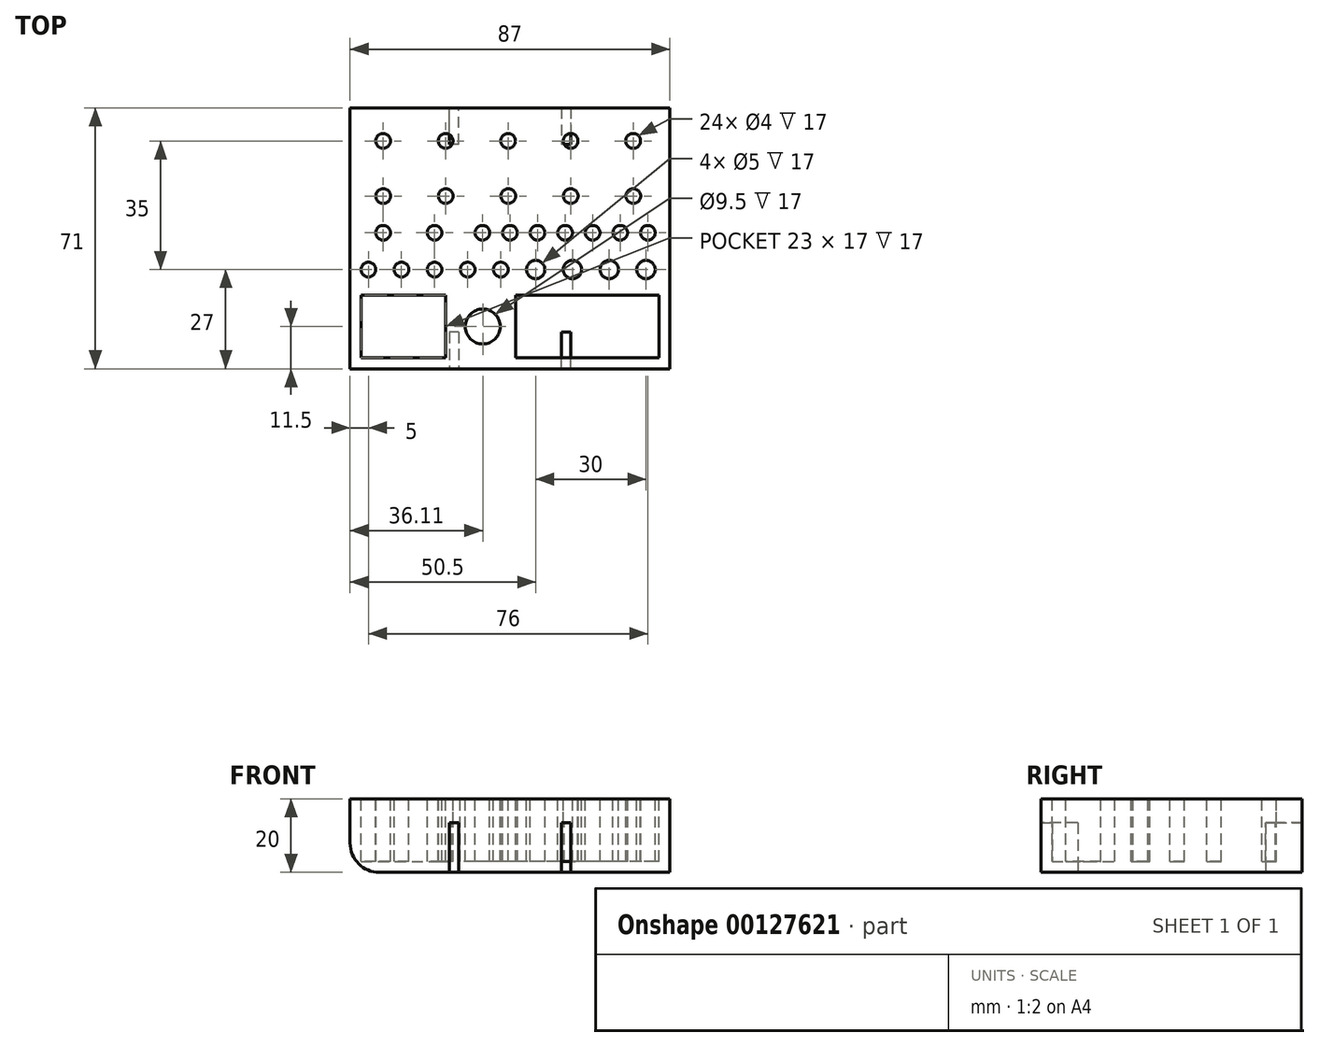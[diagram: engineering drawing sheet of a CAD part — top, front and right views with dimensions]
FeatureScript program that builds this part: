
annotation { "Feature Type Name" : "Feature", "Feature Type Description" : "" }
export const myFeature = defineFeature(function(context is Context, id is Id, definition is map)
    precondition{}
    {
        {
            var Q0;
            Q0=qCreatedBy(makeId("Top.planeOp"),FACE);
            var sketch = newSketch(context, id + "F0", { "sketchPlane" : qUnion([Q0])});
            skLineSegment(sketch, "E0.bottom", {"start": v(43.5, 35.5) * mm, "end": v(-43.5, 35.5) * mm});
            skLineSegment(sketch, "E0.top", {"start": v(43.5, -35.5) * mm, "end": v(-43.5, -35.5) * mm});
            skLineSegment(sketch, "E0.left", {"start": v(43.5, 35.5) * mm, "end": v(43.5, -35.5) * mm});
            skLineSegment(sketch, "E0.right", {"start": v(-43.5, 35.5) * mm, "end": v(-43.5, -35.5) * mm});
            skPoint(sketch, "E0.middle", {"position": v(0, 0) * mm});
            skSolve(sketch);
        }
        {
            var Q0;
            Q0=makeQuery(id+"F0.imprint","IMPRINT",FACE,{"disambiguationData":[TD([[makeQuery(id+"F0.imprint","IMPRINT",EDGE,{"derivedFrom":sQuery(id+"F0.wireOp",EDGE,"E0.bottom")}),1.0]])]});
            extrude(context, id + "F1", {"entities" : qUnion([Q0]), "depth" : 20 * mm});
        }
        {
            var Q0;
            Q0=makeQuery(id+"F1.opExtrude","CAP_FACE",FACE,{"disambiguationData":[OSD([sQuery(id+"F0.wireOp",EDGE,"E0.bottom"),sQuery(id+"F0.wireOp",EDGE,"E0.top"),sQuery(id+"F0.wireOp",EDGE,"E0.left"),sQuery(id+"F0.wireOp",EDGE,"E0.right")])],"isStart":true});
            var sketch = newSketch(context, id + "F2", { "sketchPlane" : qUnion([Q0])});
            skLineSegment(sketch, "E1.bottom", {"start": v(16.5, 35.5) * mm, "end": v(14, 35.5) * mm});
            skLineSegment(sketch, "E1.top", {"start": v(16.5, 25.5) * mm, "end": v(14, 25.5) * mm});
            skLineSegment(sketch, "E1.left", {"start": v(14, 35.5) * mm, "end": v(14, 25.5) * mm});
            skLineSegment(sketch, "E1.right", {"start": v(16.5, 35.5) * mm, "end": v(16.5, 25.5) * mm});
            skLineSegment(sketch, "E2.bottom", {"start": v(-14, 25.5) * mm, "end": v(-16.5, 25.5) * mm});
            skLineSegment(sketch, "E2.top", {"start": v(-14, 35.5) * mm, "end": v(-16.5, 35.5) * mm});
            skLineSegment(sketch, "E2.left", {"start": v(-16.5, 25.5) * mm, "end": v(-16.5, 35.5) * mm});
            skLineSegment(sketch, "E2.right", {"start": v(-14, 25.5) * mm, "end": v(-14, 35.5) * mm});
            skLineSegment(sketch, "E3", {"start": v(0, 0) * mm, "end": v(29.6, 0) * mm, "construction": true});
            skLineSegment(sketch, "E4.MirrorCS", {"start": v(-16.5, -25.5) * mm, "end": v(-16.5, -35.5) * mm});
            skLineSegment(sketch, "E5.MirrorCS", {"start": v(-14, -25.5) * mm, "end": v(-16.5, -25.5) * mm});
            skLineSegment(sketch, "E6.MirrorCS", {"start": v(16.5, -35.5) * mm, "end": v(16.5, -25.5) * mm});
            skLineSegment(sketch, "E7.MirrorCS", {"start": v(14, -35.5) * mm, "end": v(14, -25.5) * mm});
            skLineSegment(sketch, "E8.MirrorCS", {"start": v(-14, -25.5) * mm, "end": v(-14, -35.5) * mm});
            skLineSegment(sketch, "E9.MirrorCS", {"start": v(16.5, -25.5) * mm, "end": v(14, -25.5) * mm});
            skSolve(sketch);
        }
        {
            var Q0;
            Q0=makeQuery(id+"F2.imprint","IMPRINT",FACE,{"disambiguationData":[TD([[makeQuery(id+"F2.imprint","IMPRINT",EDGE,{"derivedFrom":sQuery(id+"F2.wireOp",EDGE,"E2.bottom")}),-1.0]])]});
            var Q1;
            Q1=makeQuery(id+"F2.imprint","IMPRINT",FACE,{"disambiguationData":[TD([[makeQuery(id+"F2.imprint","IMPRINT",EDGE,{"derivedFrom":sQuery(id+"F2.wireOp",EDGE,"E1.bottom")}),1.0]])]});
            var Q2;
            {var subQ0=sQuery(id+"F2.wireOp",EDGE,"E4.MirrorCS");Q2=makeQuery(id+"F2.imprint","IMPRINT",FACE,{"disambiguationData":[TD([[makeQuery(id+"F2.imprint","IMPRINT",EDGE,{"derivedFrom":subQ0}),1.0]])]});}
            var Q3;
            {var subQ0=sQuery(id+"F2.wireOp",EDGE,"E6.MirrorCS");Q3=makeQuery(id+"F2.imprint","IMPRINT",FACE,{"disambiguationData":[TD([[makeQuery(id+"F2.imprint","IMPRINT",EDGE,{"derivedFrom":subQ0}),1.0]])]});}
            extrude(context, id + "F3", {"entities" : qUnion([Q0, Q1, Q2, Q3]), "operationType" : NewBodyOperationType.REMOVE, "oppositeDirection" : true, "depth" : 13.5 * mm});
        }
        {
            var Q0;
            Q0=makeQuery(id+"F1.opExtrude","CAP_EDGE",EDGE,{"disambiguationData":[OSD([sQuery(id+"F0.wireOp",EDGE,"E0.right")])],"isStart":true});
            fillet(context, id + "F4", {"entities" : qUnion([Q0]), "radius" : 8 * mm, "tangentPropagation" : true, "allowEdgeOverflow" : false});
        }
        {
            var Q0;
            Q0=makeQuery(id+"F1.opExtrude","CAP_FACE",FACE,{"disambiguationData":[OSD([sQuery(id+"F0.wireOp",EDGE,"E0.bottom"),sQuery(id+"F0.wireOp",EDGE,"E0.top"),sQuery(id+"F0.wireOp",EDGE,"E0.left"),sQuery(id+"F0.wireOp",EDGE,"E0.right")])],"isStart":false});
            var sketch = newSketch(context, id + "F5", { "sketchPlane" : qUnion([Q0])});
            skLineSegment(sketch, "E10", {"start": v(-43.5, 35.5) * mm, "end": v(-34.5, 26.5) * mm, "construction": true});
            skCircle(sketch, "E11", {"center": v(-34.5, 26.5) * mm, "radius": 2 * mm});
            skCircle(sketch, "E12", {"center": v(-17.5, 26.5) * mm, "radius": 2 * mm});
            skCircle(sketch, "E13", {"center": v(-0.5, 26.5) * mm, "radius": 2 * mm});
            skCircle(sketch, "E14", {"center": v(16.5, 26.5) * mm, "radius": 2 * mm});
            skCircle(sketch, "E15", {"center": v(33.5, 26.5) * mm, "radius": 2 * mm});
            skCircle(sketch, "E16.1.0.0", {"center": v(-34.46, 11.5) * mm, "radius": 2 * mm});
            skCircle(sketch, "E16.1.0.1", {"center": v(-17.46, 11.5) * mm, "radius": 2 * mm});
            skCircle(sketch, "E16.1.0.2", {"center": v(-0.46, 11.5) * mm, "radius": 2 * mm});
            skCircle(sketch, "E16.1.0.3", {"center": v(16.54, 11.5) * mm, "radius": 2 * mm});
            skCircle(sketch, "E16.1.0.4", {"center": v(33.54, 11.5) * mm, "radius": 2 * mm});
            skLineSegment(sketch, "E16.direction1", {"start": v(-34.5, 26.5) * mm, "end": v(-34.46, 11.5) * mm, "construction": true});
            skCircle(sketch, "E17", {"center": v(-34.5, 1.5) * mm, "radius": 2 * mm});
            skCircle(sketch, "E18", {"center": v(-20.5, 1.5) * mm, "radius": 2 * mm});
            skCircle(sketch, "E19", {"center": v(-7.5, 1.5) * mm, "radius": 2 * mm});
            skCircle(sketch, "E20.1.0.0", {"center": v(0, 1.5) * mm, "radius": 2 * mm});
            skCircle(sketch, "E20.2.0.0", {"center": v(7.5, 1.5) * mm, "radius": 2 * mm});
            skCircle(sketch, "E20.3.0.0", {"center": v(15, 1.5) * mm, "radius": 2 * mm});
            skCircle(sketch, "E20.4.0.0", {"center": v(22.5, 1.5) * mm, "radius": 2 * mm});
            skCircle(sketch, "E20.5.0.0", {"center": v(30, 1.5) * mm, "radius": 2 * mm});
            skCircle(sketch, "E20.6.0.0", {"center": v(37.5, 1.5) * mm, "radius": 2 * mm});
            skLineSegment(sketch, "E20.direction1", {"start": v(-7.5, 1.5) * mm, "end": v(0, 1.5) * mm, "construction": true});
            skCircle(sketch, "E21", {"center": v(-38.5, -8.5) * mm, "radius": 2 * mm});
            skCircle(sketch, "E22.1.0.0", {"center": v(-29.5, -8.5) * mm, "radius": 2 * mm});
            skCircle(sketch, "E22.2.0.0", {"center": v(-20.5, -8.5) * mm, "radius": 2 * mm});
            skCircle(sketch, "E22.3.0.0", {"center": v(-11.5, -8.5) * mm, "radius": 2 * mm});
            skCircle(sketch, "E22.4.0.0", {"center": v(-2.5, -8.5) * mm, "radius": 2 * mm});
            skLineSegment(sketch, "E22.direction1", {"start": v(-38.5, -8.5) * mm, "end": v(-29.5, -8.5) * mm, "construction": true});
            skCircle(sketch, "E23", {"center": v(7, -8.5) * mm, "radius": 2.5 * mm});
            skCircle(sketch, "E24.1.0.0", {"center": v(17, -8.5) * mm, "radius": 2.5 * mm});
            skCircle(sketch, "E24.2.0.0", {"center": v(27, -8.5) * mm, "radius": 2.5 * mm});
            skCircle(sketch, "E24.3.0.0", {"center": v(37, -8.5) * mm, "radius": 2.5 * mm});
            skLineSegment(sketch, "E24.direction1", {"start": v(7, -8.5) * mm, "end": v(17, -8.5) * mm, "construction": true});
            skLineSegment(sketch, "E25.bottom", {"start": v(-40.5, -32.5) * mm, "end": v(-17.5, -32.5) * mm});
            skLineSegment(sketch, "E25.top", {"start": v(-40.5, -15.5) * mm, "end": v(-17.5, -15.5) * mm});
            skLineSegment(sketch, "E25.left", {"start": v(-40.5, -32.5) * mm, "end": v(-40.5, -15.5) * mm});
            skLineSegment(sketch, "E25.right", {"start": v(-17.5, -32.5) * mm, "end": v(-17.5, -15.5) * mm});
            skLineSegment(sketch, "E26.bottom", {"start": v(40.5, -32.5) * mm, "end": v(1.5, -32.5) * mm});
            skLineSegment(sketch, "E26.top", {"start": v(40.5, -15.5) * mm, "end": v(1.5, -15.5) * mm});
            skLineSegment(sketch, "E26.left", {"start": v(40.5, -32.5) * mm, "end": v(40.5, -15.5) * mm});
            skLineSegment(sketch, "E26.right", {"start": v(1.5, -32.5) * mm, "end": v(1.5, -15.5) * mm});
            skCircle(sketch, "E27", {"center": v(-7.4, -24) * mm, "radius": 4.75 * mm});
            skPoint(sketch, "E27.centerSnap0", {"position": v(1.5, -24) * mm});
            skSolve(sketch);
        }
        {
            var Q0;
            Q0=makeQuery(id+"F5.imprint","IMPRINT",FACE,{"disambiguationData":[TD([[makeQuery(id+"F5.imprint","IMPRINT",EDGE,{"derivedFrom":sQuery(id+"F5.wireOp",EDGE,"E25.bottom")}),1.0]])]});
            var Q1;
            Q1=makeQuery(id+"F5.imprint","IMPRINT",FACE,{"disambiguationData":[TD([[makeQuery(id+"F5.imprint","IMPRINT",EDGE,{"derivedFrom":sQuery(id+"F5.wireOp",EDGE,"E26.bottom")}),-1.0]])]});
            var Q2;
            Q2=makeQuery(id+"F5.imprint","IMPRINT",FACE,{"disambiguationData":[TD([[makeQuery(id+"F5.imprint","IMPRINT",EDGE,{"derivedFrom":sQuery(id+"F5.wireOp",EDGE,"E27")}),1.0]])]});
            var Q3;
            Q3=makeQuery(id+"F5.imprint","IMPRINT",FACE,{"disambiguationData":[TD([[makeQuery(id+"F5.imprint","IMPRINT",EDGE,{"derivedFrom":sQuery(id+"F5.wireOp",EDGE,"E21")}),1.0]])]});
            var Q4;
            Q4=makeQuery(id+"F5.imprint","IMPRINT",FACE,{"disambiguationData":[TD([[makeQuery(id+"F5.imprint","IMPRINT",EDGE,{"derivedFrom":sQuery(id+"F5.wireOp",EDGE,"E22.1.0.0")}),1.0]])]});
            var Q5;
            Q5=makeQuery(id+"F5.imprint","IMPRINT",FACE,{"disambiguationData":[TD([[makeQuery(id+"F5.imprint","IMPRINT",EDGE,{"derivedFrom":sQuery(id+"F5.wireOp",EDGE,"E22.2.0.0")}),1.0]])]});
            var Q6;
            Q6=makeQuery(id+"F5.imprint","IMPRINT",FACE,{"disambiguationData":[TD([[makeQuery(id+"F5.imprint","IMPRINT",EDGE,{"derivedFrom":sQuery(id+"F5.wireOp",EDGE,"E22.3.0.0")}),1.0]])]});
            var Q7;
            Q7=makeQuery(id+"F5.imprint","IMPRINT",FACE,{"disambiguationData":[TD([[makeQuery(id+"F5.imprint","IMPRINT",EDGE,{"derivedFrom":sQuery(id+"F5.wireOp",EDGE,"E22.4.0.0")}),1.0]])]});
            var Q8;
            Q8=makeQuery(id+"F5.imprint","IMPRINT",FACE,{"disambiguationData":[TD([[makeQuery(id+"F5.imprint","IMPRINT",EDGE,{"derivedFrom":sQuery(id+"F5.wireOp",EDGE,"E23")}),1.0]])]});
            var Q9;
            Q9=makeQuery(id+"F5.imprint","IMPRINT",FACE,{"disambiguationData":[TD([[makeQuery(id+"F5.imprint","IMPRINT",EDGE,{"derivedFrom":sQuery(id+"F5.wireOp",EDGE,"E24.1.0.0")}),1.0]])]});
            var Q10;
            Q10=makeQuery(id+"F5.imprint","IMPRINT",FACE,{"disambiguationData":[TD([[makeQuery(id+"F5.imprint","IMPRINT",EDGE,{"derivedFrom":sQuery(id+"F5.wireOp",EDGE,"E24.2.0.0")}),1.0]])]});
            var Q11;
            Q11=makeQuery(id+"F5.imprint","IMPRINT",FACE,{"disambiguationData":[TD([[makeQuery(id+"F5.imprint","IMPRINT",EDGE,{"derivedFrom":sQuery(id+"F5.wireOp",EDGE,"E24.3.0.0")}),1.0]])]});
            var Q12;
            Q12=makeQuery(id+"F5.imprint","IMPRINT",FACE,{"disambiguationData":[TD([[makeQuery(id+"F5.imprint","IMPRINT",EDGE,{"derivedFrom":sQuery(id+"F5.wireOp",EDGE,"E20.6.0.0")}),1.0]])]});
            var Q13;
            Q13=makeQuery(id+"F5.imprint","IMPRINT",FACE,{"disambiguationData":[TD([[makeQuery(id+"F5.imprint","IMPRINT",EDGE,{"derivedFrom":sQuery(id+"F5.wireOp",EDGE,"E20.5.0.0")}),1.0]])]});
            var Q14;
            Q14=makeQuery(id+"F5.imprint","IMPRINT",FACE,{"disambiguationData":[TD([[makeQuery(id+"F5.imprint","IMPRINT",EDGE,{"derivedFrom":sQuery(id+"F5.wireOp",EDGE,"E20.4.0.0")}),1.0]])]});
            var Q15;
            Q15=makeQuery(id+"F5.imprint","IMPRINT",FACE,{"disambiguationData":[TD([[makeQuery(id+"F5.imprint","IMPRINT",EDGE,{"derivedFrom":sQuery(id+"F5.wireOp",EDGE,"E20.3.0.0")}),1.0]])]});
            var Q16;
            Q16=makeQuery(id+"F5.imprint","IMPRINT",FACE,{"disambiguationData":[TD([[makeQuery(id+"F5.imprint","IMPRINT",EDGE,{"derivedFrom":sQuery(id+"F5.wireOp",EDGE,"E20.2.0.0")}),1.0]])]});
            var Q17;
            Q17=makeQuery(id+"F5.imprint","IMPRINT",FACE,{"disambiguationData":[TD([[makeQuery(id+"F5.imprint","IMPRINT",EDGE,{"derivedFrom":sQuery(id+"F5.wireOp",EDGE,"E20.1.0.0")}),1.0]])]});
            var Q18;
            Q18=makeQuery(id+"F5.imprint","IMPRINT",FACE,{"disambiguationData":[TD([[makeQuery(id+"F5.imprint","IMPRINT",EDGE,{"derivedFrom":sQuery(id+"F5.wireOp",EDGE,"E19")}),1.0]])]});
            var Q19;
            Q19=makeQuery(id+"F5.imprint","IMPRINT",FACE,{"disambiguationData":[TD([[makeQuery(id+"F5.imprint","IMPRINT",EDGE,{"derivedFrom":sQuery(id+"F5.wireOp",EDGE,"E18")}),1.0]])]});
            var Q20;
            Q20=makeQuery(id+"F5.imprint","IMPRINT",FACE,{"disambiguationData":[TD([[makeQuery(id+"F5.imprint","IMPRINT",EDGE,{"derivedFrom":sQuery(id+"F5.wireOp",EDGE,"E17")}),1.0]])]});
            var Q21;
            Q21=makeQuery(id+"F5.imprint","IMPRINT",FACE,{"disambiguationData":[TD([[makeQuery(id+"F5.imprint","IMPRINT",EDGE,{"derivedFrom":sQuery(id+"F5.wireOp",EDGE,"E16.1.0.0")}),1.0]])]});
            var Q22;
            Q22=makeQuery(id+"F5.imprint","IMPRINT",FACE,{"disambiguationData":[TD([[makeQuery(id+"F5.imprint","IMPRINT",EDGE,{"derivedFrom":sQuery(id+"F5.wireOp",EDGE,"E11")}),1.0]])]});
            var Q23;
            Q23=makeQuery(id+"F5.imprint","IMPRINT",FACE,{"disambiguationData":[TD([[makeQuery(id+"F5.imprint","IMPRINT",EDGE,{"derivedFrom":sQuery(id+"F5.wireOp",EDGE,"E12")}),1.0]])]});
            var Q24;
            Q24=makeQuery(id+"F5.imprint","IMPRINT",FACE,{"disambiguationData":[TD([[makeQuery(id+"F5.imprint","IMPRINT",EDGE,{"derivedFrom":sQuery(id+"F5.wireOp",EDGE,"E16.1.0.1")}),1.0]])]});
            var Q25;
            Q25=makeQuery(id+"F5.imprint","IMPRINT",FACE,{"disambiguationData":[TD([[makeQuery(id+"F5.imprint","IMPRINT",EDGE,{"derivedFrom":sQuery(id+"F5.wireOp",EDGE,"E16.1.0.2")}),1.0]])]});
            var Q26;
            Q26=makeQuery(id+"F5.imprint","IMPRINT",FACE,{"disambiguationData":[TD([[makeQuery(id+"F5.imprint","IMPRINT",EDGE,{"derivedFrom":sQuery(id+"F5.wireOp",EDGE,"E13")}),1.0]])]});
            var Q27;
            Q27=makeQuery(id+"F5.imprint","IMPRINT",FACE,{"disambiguationData":[TD([[makeQuery(id+"F5.imprint","IMPRINT",EDGE,{"derivedFrom":sQuery(id+"F5.wireOp",EDGE,"E14")}),1.0]])]});
            var Q28;
            Q28=makeQuery(id+"F5.imprint","IMPRINT",FACE,{"disambiguationData":[TD([[makeQuery(id+"F5.imprint","IMPRINT",EDGE,{"derivedFrom":sQuery(id+"F5.wireOp",EDGE,"E16.1.0.3")}),1.0]])]});
            var Q29;
            Q29=makeQuery(id+"F5.imprint","IMPRINT",FACE,{"disambiguationData":[TD([[makeQuery(id+"F5.imprint","IMPRINT",EDGE,{"derivedFrom":sQuery(id+"F5.wireOp",EDGE,"E16.1.0.4")}),1.0]])]});
            var Q30;
            Q30=makeQuery(id+"F5.imprint","IMPRINT",FACE,{"disambiguationData":[TD([[makeQuery(id+"F5.imprint","IMPRINT",EDGE,{"derivedFrom":sQuery(id+"F5.wireOp",EDGE,"E15")}),1.0]])]});
            extrude(context, id + "F6", {"entities" : qUnion([Q0, Q1, Q2, Q3, Q4, Q5, Q6, Q7, Q8, Q9, Q10, Q11, Q12, Q13, Q14, Q15, Q16, Q17, Q18, Q19, Q20, Q21, Q22, Q23, Q24, Q25, Q26, Q27, Q28, Q29, Q30]), "operationType" : NewBodyOperationType.REMOVE, "oppositeDirection" : true, "depth" : 17 * mm});
        }
    });
